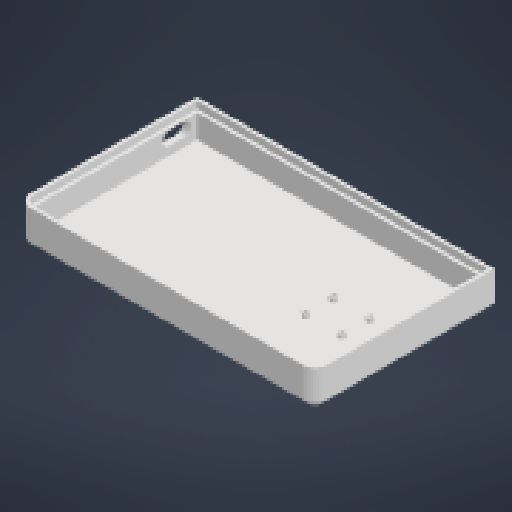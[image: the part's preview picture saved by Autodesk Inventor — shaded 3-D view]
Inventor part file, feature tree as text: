
AUTODESK INVENTOR PART (.ipt)
format: ipt  version: 2024 (Build 280153000, 153)  size: 388,096 bytes
history: native  units: mm
features: extrude x11, sketch x11, projected_geometry x11, other x5, chamfer x2, fillet x1, shell x1, reference x1
ambient origin geometry x8: Origin, YZ Plane, XZ Plane, XY Plane, X Axis, Y Axis, Z Axis, Center Point
bodies: Body1 (feature_tree), Body2 (feature_tree)
feature tree (43):
  other  "솔리드1"
  extrude  "돌출1"  Depth=217.0mm
  extrude  "돌출7"  Depth=131.0mm
  extrude  "돌출8"  Depth=27.0mm TaperAngle=0.0deg
  fillet  "모깎기5"  Radius=50.0mm
  chamfer  "모따기3"  Distance=27.0mm
  shell  "쉘3"  Thickness=154.0mm
  extrude  "돌출11"  Depth=10.0mm
  extrude  "돌출12"  Depth=23.0mm TaperAngle=45.0deg
  chamfer  "모따기4"  Distance=10.0mm
  extrude  "돌출13"  Depth=5.0mm TaperAngle=0.0deg
  extrude  "돌출14"  Depth=5.0mm TaperAngle=0.0deg
  extrude  "돌출15"  Depth=10.0mm TaperAngle=45.0deg
  extrude  "돌출16"  Depth=50.0mm
  extrude  "돌출17"  Depth=50.0mm
  extrude  "돌출18"  Depth=197.0mm
  sketch  "스케치1"
  sketch  "스케치8"
  projected_geometry  "투영된 루프3"
  sketch  "스케치9"
  sketch  "스케치12"
  projected_geometry  "투영된 루프6"
  sketch  "스케치13"
  projected_geometry  "투영된 루프7"
  sketch  "스케치15"
  projected_geometry  "투영된 루프8"
  projected_geometry  "투영된 루프9"
  sketch  "스케치17"
  projected_geometry  "투영된 루프11"
  sketch  "스케치21"
  projected_geometry  "투영된 루프14"
  sketch  "스케치22"
  projected_geometry  "투영된 루프15"
  sketch  "스케치23"
  projected_geometry  "투영된 루프16"
  projected_geometry  "투영된 루프17"
  sketch  "스케치24"
  projected_geometry  "투영된 루프18"
  reference  "참조1"
  other  "<userpath>\Downloads\AAST\PART\AAST Remote Controler\AASTRC case.iam"
  other  "AASTRC case.iam"
  other  "AASTRC Middle case cover assembly:1"
  other  "AASTRC Middle case cover:1"
